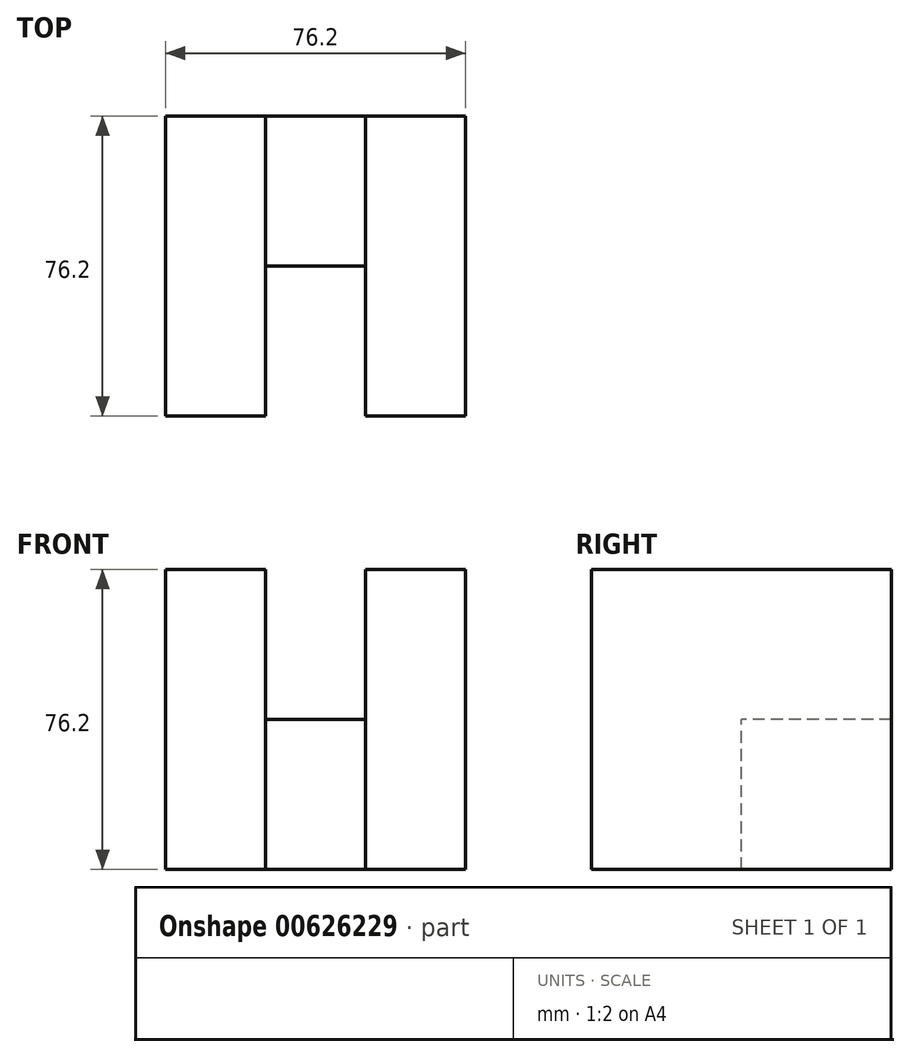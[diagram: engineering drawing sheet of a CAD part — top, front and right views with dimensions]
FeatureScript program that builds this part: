
annotation { "Feature Type Name" : "Feature", "Feature Type Description" : "" }
export const myFeature = defineFeature(function(context is Context, id is Id, definition is map)
    precondition{}
    {
        {
            var Q0;
            Q0=qCreatedBy(makeId("Right.planeOp"),FACE);
            var sketch = newSketch(context, id + "F0", { "sketchPlane" : qUnion([Q0])});
            skLineSegment(sketch, "E0.bottom", {"start": v(38.1, 38.1) * mm, "end": v(-38.1, 38.1) * mm});
            skLineSegment(sketch, "E0.top", {"start": v(38.1, -38.1) * mm, "end": v(-38.1, -38.1) * mm});
            skLineSegment(sketch, "E0.left", {"start": v(38.1, 38.1) * mm, "end": v(38.1, -38.1) * mm});
            skLineSegment(sketch, "E0.right", {"start": v(-38.1, 38.1) * mm, "end": v(-38.1, -38.1) * mm});
            skPoint(sketch, "E0.middle", {"position": v(0, 0) * mm});
            skSolve(sketch);
        }
        {
            var Q0;
            Q0 = qSketchRegion(id + "F0", true);
            extrude(context, id + "F1", {"entities" : qUnion([Q0]), "depth" : 25.4 * mm, "offsetDistance" : 25.4 * mm});
        }
        {
            var Q0;
            Q0=makeQuery(id+"F1.opExtrude","CAP_FACE",FACE,{"disambiguationData":[OSD([sQuery(id+"F0.wireOp",EDGE,"E0.bottom"),sQuery(id+"F0.wireOp",EDGE,"E0.top"),sQuery(id+"F0.wireOp",EDGE,"E0.left"),sQuery(id+"F0.wireOp",EDGE,"E0.right")])],"isStart":false});
            var sketch = newSketch(context, id + "F2", { "sketchPlane" : qUnion([Q0])});
            skLineSegment(sketch, "E1.bottom", {"start": v(38.1, -38.1) * mm, "end": v(0, -38.1) * mm});
            skLineSegment(sketch, "E1.top", {"start": v(38.1, 0) * mm, "end": v(0, 0) * mm});
            skLineSegment(sketch, "E1.left", {"start": v(38.1, -38.1) * mm, "end": v(38.1, 0) * mm});
            skLineSegment(sketch, "E1.right", {"start": v(0, -38.1) * mm, "end": v(0, 0) * mm});
            skSolve(sketch);
        }
        {
            var Q0;
            Q0 = qSketchRegion(id + "F2", true);
            extrude(context, id + "F3", {"entities" : qUnion([Q0]), "operationType" : NewBodyOperationType.ADD, "depth" : 25.4 * mm, "offsetDistance" : 25.4 * mm});
        }
        {
            var Q0;
            Q0=makeQuery(id+"F3.opExtrude","CAP_FACE",FACE,{"disambiguationData":[OSD([sQuery(id+"F2.wireOp",EDGE,"E1.bottom"),sQuery(id+"F2.wireOp",EDGE,"E1.top"),sQuery(id+"F2.wireOp",EDGE,"E1.left"),sQuery(id+"F2.wireOp",EDGE,"E1.right")])],"isStart":false});
            var sketch = newSketch(context, id + "F4", { "sketchPlane" : qUnion([Q0])});
            skLineSegment(sketch, "E2.bottom", {"start": v(38.1, -38.1) * mm, "end": v(-38.1, -38.1) * mm});
            skLineSegment(sketch, "E2.top", {"start": v(38.1, 38.1) * mm, "end": v(-38.1, 38.1) * mm});
            skLineSegment(sketch, "E2.left", {"start": v(38.1, -38.1) * mm, "end": v(38.1, 38.1) * mm});
            skLineSegment(sketch, "E2.right", {"start": v(-38.1, -38.1) * mm, "end": v(-38.1, 38.1) * mm});
            skSolve(sketch);
        }
        {
            var Q0;
            Q0 = qSketchRegion(id + "F4", true);
            extrude(context, id + "F5", {"entities" : qUnion([Q0]), "operationType" : NewBodyOperationType.ADD, "depth" : 25.4 * mm, "offsetDistance" : 25.4 * mm});
        }
    });
